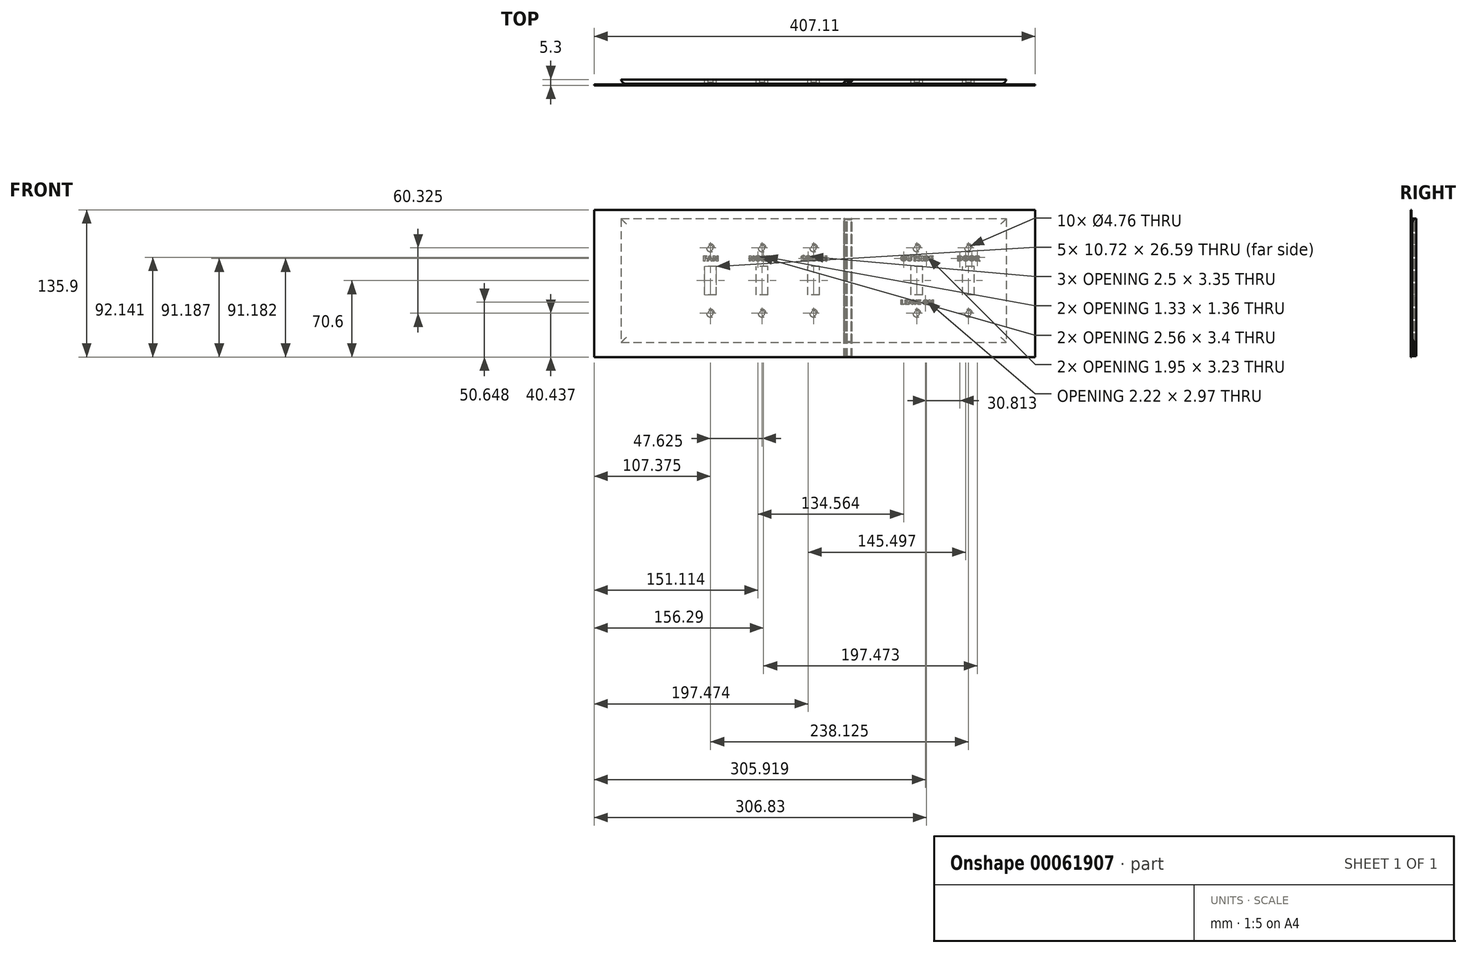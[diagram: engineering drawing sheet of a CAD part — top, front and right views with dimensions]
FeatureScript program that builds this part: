
annotation { "Feature Type Name" : "Feature", "Feature Type Description" : "" }
export const myFeature = defineFeature(function(context is Context, id is Id, definition is map)
    precondition{}
    {
        {
            var Q0;
            Q0=qCreatedBy(makeId("Front.planeOp"),FACE);
            var sketch = newSketch(context, id + "F0", { "sketchPlane" : qUnion([Q0])});
            skLineSegment(sketch, "E0.left", {"start": v(-320.68, 57.15) * mm, "end": v(-320.68, -57.15) * mm});
            skLineSegment(sketch, "E0.right", {"start": v(34.93, 57.15) * mm, "end": v(34.92, -57.15) * mm});
            skPoint(sketch, "E1", {"position": v(0, 57.15) * mm});
            skPoint(sketch, "E2", {"position": v(34.92, 0) * mm});
            skLineSegment(sketch, "E3.rect.bottom", {"start": v(5.36, -13.3) * mm, "end": v(-5.36, -13.3) * mm});
            skLineSegment(sketch, "E3.rect.top", {"start": v(5.36, 13.3) * mm, "end": v(-5.36, 13.3) * mm});
            skLineSegment(sketch, "E3.rect.left", {"start": v(5.36, -13.3) * mm, "end": v(5.36, 13.3) * mm});
            skLineSegment(sketch, "E3.rect.right", {"start": v(-5.36, -13.3) * mm, "end": v(-5.36, 13.3) * mm});
            skPoint(sketch, "E3.rect.middle", {"position": v(0, 0) * mm});
            skCircle(sketch, "E4", {"center": v(0, 30.16) * mm, "radius": 2.38 * mm});
            skLineSegment(sketch, "E5", {"start": v(43.2, 0) * mm, "end": v(-149.72, 0) * mm, "construction": true});
            skCircle(sketch, "E6.MirrorC", {"center": v(0, -30.16) * mm, "radius": 2.38 * mm});
            skLineSegment(sketch, "E7", {"start": v(-320.68, 57.15) * mm, "end": v(34.93, 57.15) * mm});
            skLineSegment(sketch, "E8", {"start": v(-320.68, -57.15) * mm, "end": v(34.92, -57.15) * mm});
            skLineSegment(sketch, "E9.rect.left", {"start": v(-42.27, -13.3) * mm, "end": v(-42.27, 13.3) * mm});
            skLineSegment(sketch, "E9.rect.right", {"start": v(-52.98, -13.3) * mm, "end": v(-52.98, 13.3) * mm});
            skPoint(sketch, "E9.rect.middle", {"position": v(-47.63, 0) * mm});
            skCircle(sketch, "E10", {"center": v(-47.63, 30.16) * mm, "radius": 2.38 * mm});
            skCircle(sketch, "E11.MirrorC", {"center": v(-47.63, -30.16) * mm, "radius": 2.38 * mm});
            skLineSegment(sketch, "E9.rect.bottom", {"start": v(-42.27, -13.3) * mm, "end": v(-52.98, -13.3) * mm});
            skLineSegment(sketch, "E9.rect.top", {"start": v(-42.27, 13.3) * mm, "end": v(-52.98, 13.3) * mm});
            skLineSegment(sketch, "E12.rect.left", {"start": v(-137.52, -13.3) * mm, "end": v(-137.52, 13.3) * mm});
            skLineSegment(sketch, "E12.rect.right", {"start": v(-148.23, -13.3) * mm, "end": v(-148.23, 13.3) * mm});
            skPoint(sketch, "E12.rect.middle", {"position": v(-142.88, 0) * mm});
            skCircle(sketch, "E13", {"center": v(-142.88, 30.16) * mm, "radius": 2.38 * mm});
            skCircle(sketch, "E14.MirrorC", {"center": v(-142.88, -30.16) * mm, "radius": 2.38 * mm});
            skLineSegment(sketch, "E12.rect.bottom", {"start": v(-137.52, -13.3) * mm, "end": v(-148.23, -13.3) * mm});
            skLineSegment(sketch, "E12.rect.top", {"start": v(-137.52, 13.3) * mm, "end": v(-148.23, 13.3) * mm});
            skLineSegment(sketch, "E15.rect.left", {"start": v(-185.14, -13.3) * mm, "end": v(-185.14, 13.3) * mm});
            skLineSegment(sketch, "E15.rect.right", {"start": v(-195.86, -13.3) * mm, "end": v(-195.86, 13.3) * mm});
            skPoint(sketch, "E15.rect.middle", {"position": v(-190.5, 0) * mm});
            skCircle(sketch, "E16", {"center": v(-190.5, 30.16) * mm, "radius": 2.38 * mm});
            skCircle(sketch, "E17.MirrorC", {"center": v(-190.5, -30.16) * mm, "radius": 2.38 * mm});
            skLineSegment(sketch, "E15.rect.bottom", {"start": v(-185.14, -13.3) * mm, "end": v(-195.86, -13.3) * mm});
            skLineSegment(sketch, "E15.rect.top", {"start": v(-185.14, 13.3) * mm, "end": v(-195.86, 13.3) * mm});
            skLineSegment(sketch, "E18.rect.left", {"start": v(-232.77, -13.3) * mm, "end": v(-232.77, 13.3) * mm});
            skLineSegment(sketch, "E18.rect.right", {"start": v(-243.48, -13.3) * mm, "end": v(-243.48, 13.3) * mm});
            skPoint(sketch, "E18.rect.middle", {"position": v(-238.13, 0) * mm});
            skCircle(sketch, "E19", {"center": v(-238.13, 30.16) * mm, "radius": 2.38 * mm});
            skCircle(sketch, "E20.MirrorC", {"center": v(-238.13, -30.16) * mm, "radius": 2.38 * mm});
            skLineSegment(sketch, "E18.rect.bottom", {"start": v(-232.77, -13.3) * mm, "end": v(-243.48, -13.3) * mm});
            skLineSegment(sketch, "E18.rect.top", {"start": v(-232.77, 13.3) * mm, "end": v(-243.48, 13.3) * mm});
            skLineSegment(sketch, "E21", {"start": v(-243.48, 13.3) * mm, "end": v(-195.86, 13.3) * mm, "construction": true});
            skLineSegment(sketch, "E22", {"start": v(-195.86, 13.3) * mm, "end": v(-148.23, 13.3) * mm, "construction": true});
            skLineSegment(sketch, "E23", {"start": v(-52.98, 13.3) * mm, "end": v(-5.36, 13.3) * mm, "construction": true});
            skSolve(sketch);
        }
        {
            var Q0;
            Q0=makeQuery(id+"F0.imprint","IMPRINT",FACE,{"disambiguationData":[TD([[makeQuery(id+"F0.imprint","IMPRINT",EDGE,{"derivedFrom":sQuery(id+"F0.wireOp",EDGE,"E0.left")}),1.0]])]});
            extrude(context, id + "F1", {"entities" : qUnion([Q0]), "depth" : 3.97 * mm});
        }
        {
            var Q0;
            Q0=makeQuery(id+"F1.opExtrude","SWEPT_FACE",FACE,{"disambiguationData":[OSD([sQuery(id+"F0.wireOp",EDGE,"E7")])]});
            var sketch = newSketch(context, id + "F2", { "sketchPlane" : qUnion([Q0])});
            skArc(sketch, "E24", {"start": v(-114.3, -1.98) * mm, "mid": v(-114.79, -2.98) * mm, "end": v(-114.3, -3.97) * mm});
            skArc(sketch, "E25", {"start": v(-107.95, -1.98) * mm, "mid": v(-107.46, -1) * mm, "end": v(-107.95, 0) * mm});
            skLineSegment(sketch, "E26", {"start": v(-111.12, 0) * mm, "end": v(-111.12, -3.97) * mm, "construction": true});
            skPoint(sketch, "E27", {"position": v(-111.12, -1.98) * mm});
            skLineSegment(sketch, "E28", {"start": v(-114.3, -1.98) * mm, "end": v(-113.53, -1.98) * mm, "construction": true});
            skLineSegment(sketch, "E29", {"start": v(-111.12, -1.98) * mm, "end": v(-108.72, -1.98) * mm, "construction": true});
            skLineSegment(sketch, "E30", {"start": v(-113.53, -1.98) * mm, "end": v(-111.12, -1.98) * mm, "construction": true});
            skLineSegment(sketch, "E31", {"start": v(-108.72, -1.98) * mm, "end": v(-107.95, -1.98) * mm, "construction": true});
            skLineSegment(sketch, "E32", {"start": v(-114.3, -1.98) * mm, "end": v(-113.53, -1.98) * mm});
            skLineSegment(sketch, "E33", {"start": v(-113.53, -1.98) * mm, "end": v(-113.29, -1.43) * mm});
            skLineSegment(sketch, "E34", {"start": v(-113.29, -1.43) * mm, "end": v(-112.27, -1.43) * mm});
            skLineSegment(sketch, "E35", {"start": v(-112.27, -1.43) * mm, "end": v(-111.95, -1.98) * mm});
            skLineSegment(sketch, "E36", {"start": v(-111.95, -1.98) * mm, "end": v(-107.95, -1.98) * mm});
            skArc(sketch, "E37.0", {"start": v(-114.36, -1.8) * mm, "mid": v(-114.96, -2.84) * mm, "end": v(-114.57, -3.97) * mm});
            skLineSegment(sketch, "E37.1", {"start": v(-114.36, -1.8) * mm, "end": v(-113.65, -1.8) * mm});
            skLineSegment(sketch, "E37.2", {"start": v(-113.65, -1.8) * mm, "end": v(-113.4, -1.25) * mm});
            skArc(sketch, "E37.3", {"start": v(-108.01, -1.8) * mm, "mid": v(-107.65, -0.82) * mm, "end": v(-108.3, 0) * mm});
            skLineSegment(sketch, "E37.4", {"start": v(-111.85, -1.8) * mm, "end": v(-108.01, -1.8) * mm});
            skLineSegment(sketch, "E37.5", {"start": v(-112.17, -1.25) * mm, "end": v(-111.85, -1.8) * mm});
            skLineSegment(sketch, "E37.6", {"start": v(-113.4, -1.25) * mm, "end": v(-112.17, -1.25) * mm});
            skLineSegment(sketch, "E38", {"start": v(-114.57, -3.97) * mm, "end": v(-114.3, -3.97) * mm});
            skLineSegment(sketch, "E39", {"start": v(-108.3, 0) * mm, "end": v(-107.95, 0) * mm});
            skSolve(sketch);
        }
        {
            var Q0;
            Q0 = qSketchRegion(id + "F2", true);
            extrude(context, id + "F3", {"entities" : qUnion([Q0]), "oppositeDirection" : true, "depth" : 127 * mm});
        }
        {
            var Q0;
            Q0=makeQuery(id+"F1.opExtrude","CAP_EDGE",EDGE,{"disambiguationData":[OSD([sQuery(id+"F0.wireOp",EDGE,"E7")])],"isStart":false});
            var Q1;
            Q1=makeQuery(id+"F1.opExtrude","CAP_EDGE",EDGE,{"disambiguationData":[OSD([sQuery(id+"F0.wireOp",EDGE,"E8")])],"isStart":false});
            var Q2;
            Q2=makeQuery(id+"F1.opExtrude","CAP_EDGE",EDGE,{"disambiguationData":[OSD([sQuery(id+"F0.wireOp",EDGE,"E0.right")])],"isStart":false});
            var Q3;
            Q3=makeQuery(id+"F1.opExtrude","CAP_EDGE",EDGE,{"disambiguationData":[OSD([sQuery(id+"F0.wireOp",EDGE,"E0.left")])],"isStart":false});
            fillet(context, id + "F4", {"entities" : qUnion([Q0, Q1, Q2, Q3]), "radius" : 5.08 * mm, "tangentPropagation" : true, "allowEdgeOverflow" : false});
        }
        {
            var Q0;
            Q0=makeQuery(id+"F3.opExtrude","SWEPT_BODY",BODY,{"disambiguationData":[OSD([sQuery(id+"F2.wireOp",EDGE,"E24"),sQuery(id+"F2.wireOp",EDGE,"E25"),sQuery(id+"F2.wireOp",EDGE,"E32"),sQuery(id+"F2.wireOp",EDGE,"E33"),sQuery(id+"F2.wireOp",EDGE,"E34"),sQuery(id+"F2.wireOp",EDGE,"E35"),sQuery(id+"F2.wireOp",EDGE,"E36"),sQuery(id+"F2.wireOp",EDGE,"E37.0"),sQuery(id+"F2.wireOp",EDGE,"E37.1"),sQuery(id+"F2.wireOp",EDGE,"E37.2"),sQuery(id+"F2.wireOp",EDGE,"E37.3"),sQuery(id+"F2.wireOp",EDGE,"E37.4"),sQuery(id+"F2.wireOp",EDGE,"E37.5"),sQuery(id+"F2.wireOp",EDGE,"E37.6"),sQuery(id+"F2.wireOp",EDGE,"E38"),sQuery(id+"F2.wireOp",EDGE,"E39")])]});
            var Q1;
            Q1=makeQuery(id+"F1.opExtrude","SWEPT_BODY",BODY,{"disambiguationData":[OSD([sQuery(id+"F0.wireOp",EDGE,"E0.right"),sQuery(id+"F0.wireOp",EDGE,"E3.rect.bottom"),sQuery(id+"F0.wireOp",EDGE,"E3.rect.top"),sQuery(id+"F0.wireOp",EDGE,"E3.rect.left"),sQuery(id+"F0.wireOp",EDGE,"E3.rect.right"),sQuery(id+"F0.wireOp",EDGE,"E4"),sQuery(id+"F0.wireOp",EDGE,"E6.MirrorC"),sQuery(id+"F0.wireOp",EDGE,"E7"),sQuery(id+"F0.wireOp",EDGE,"E8"),sQuery(id+"F0.wireOp",EDGE,"E9.rect.left"),sQuery(id+"F0.wireOp",EDGE,"E9.rect.right"),sQuery(id+"F0.wireOp",EDGE,"E10"),sQuery(id+"F0.wireOp",EDGE,"E11.MirrorC"),sQuery(id+"F0.wireOp",EDGE,"E9.rect.bottom"),sQuery(id+"F0.wireOp",EDGE,"E9.rect.top"),sQuery(id+"F0.wireOp",EDGE,"6Bv0av7S-DaCH-K0Nu-mwO3-w7JLu1CZrWGv")])]});
            booleanBodies(context, id + "F5", {"operationType" : BooleanOperationType.SUBTRACTION, "tools" : qUnion([Q0]), "targets" : qUnion([Q1]), "keepTools" : true});
        }
        {
            var Q0;
            Q0=makeQuery(id+"F1.opExtrude","CAP_EDGE",EDGE,{"disambiguationData":[OSD([sQuery(id+"F0.wireOp",EDGE,"E4")])],"isStart":false});
            var Q1;
            Q1=makeQuery(id+"F1.opExtrude","CAP_EDGE",EDGE,{"disambiguationData":[OSD([sQuery(id+"F0.wireOp",EDGE,"E10")])],"isStart":false});
            var Q2;
            Q2=makeQuery(id+"F1.opExtrude","CAP_EDGE",EDGE,{"disambiguationData":[OSD([sQuery(id+"F0.wireOp",EDGE,"E6.MirrorC")])],"isStart":false});
            var Q3;
            Q3=makeQuery(id+"F1.opExtrude","CAP_EDGE",EDGE,{"disambiguationData":[OSD([sQuery(id+"F0.wireOp",EDGE,"E11.MirrorC")])],"isStart":false});
            var Q4;
            Q4=makeQuery(id+"F1.opExtrude","CAP_EDGE",EDGE,{"disambiguationData":[OSD([sQuery(id+"F0.wireOp",EDGE,"E14.MirrorC")])],"isStart":false});
            var Q5;
            Q5=makeQuery(id+"F1.opExtrude","CAP_EDGE",EDGE,{"disambiguationData":[OSD([sQuery(id+"F0.wireOp",EDGE,"E17.MirrorC")])],"isStart":false});
            var Q6;
            Q6=makeQuery(id+"F1.opExtrude","CAP_EDGE",EDGE,{"disambiguationData":[OSD([sQuery(id+"F0.wireOp",EDGE,"E20.MirrorC")])],"isStart":false});
            var Q7;
            Q7=makeQuery(id+"F1.opExtrude","CAP_EDGE",EDGE,{"disambiguationData":[OSD([sQuery(id+"F0.wireOp",EDGE,"E16")])],"isStart":false});
            var Q8;
            Q8=makeQuery(id+"F1.opExtrude","CAP_EDGE",EDGE,{"disambiguationData":[OSD([sQuery(id+"F0.wireOp",EDGE,"E13")])],"isStart":false});
            var Q9;
            Q9=makeQuery(id+"F1.opExtrude","CAP_EDGE",EDGE,{"disambiguationData":[OSD([sQuery(id+"F0.wireOp",EDGE,"E19")])],"isStart":false});
            chamfer(context, id + "F6", {"entities" : qUnion([Q0, Q1, Q2, Q3, Q4, Q5, Q6, Q7, Q8, Q9]), "width" : 1.27 * mm, "tangentPropagation" : true});
        }
        {
            var Q0;
            {var subQ0=sQuery(id+"F0.wireOp",EDGE,"E17.MirrorC");var subQ1=sQuery(id+"F0.wireOp",EDGE,"E15.rect.bottom");var subQ2=sQuery(id+"F0.wireOp",EDGE,"E18.rect.bottom");var subQ3=sQuery(id+"F0.wireOp",EDGE,"E15.rect.left");var subQ4=sQuery(id+"F0.wireOp",EDGE,"E12.rect.top");var subQ5=sQuery(id+"F0.wireOp",EDGE,"E16");var subQ6=sQuery(id+"F0.wireOp",EDGE,"E20.MirrorC");var subQ7=sQuery(id+"F0.wireOp",EDGE,"E15.rect.right");var subQ8=sQuery(id+"F0.wireOp",EDGE,"E19");var subQ9=sQuery(id+"F0.wireOp",EDGE,"E12.rect.left");var subQ10=sQuery(id+"F0.wireOp",EDGE,"E18.rect.top");var subQ11=sQuery(id+"F0.wireOp",EDGE,"E12.rect.bottom");var subQ12=sQuery(id+"F0.wireOp",EDGE,"E12.rect.right");var subQ13=sQuery(id+"F0.wireOp",EDGE,"E13");var subQ14=sQuery(id+"F0.wireOp",EDGE,"E8");var subQ15=sQuery(id+"F0.wireOp",EDGE,"E14.MirrorC");var subQ16=sQuery(id+"F0.wireOp",EDGE,"E15.rect.top");var subQ17=sQuery(id+"F0.wireOp",EDGE,"E18.rect.left");var subQ18=sQuery(id+"F0.wireOp",EDGE,"E18.rect.right");var subQ19=sQuery(id+"F0.wireOp",EDGE,"E0.left");var subQ20=sQuery(id+"F0.wireOp",EDGE,"E7");Q0=makeQuery(id+"F5.opBoolean","SPLIT",FACE,{"disambiguationData":[TD([makeQuery(id+"F1.opExtrude","SWEPT_FACE",FACE,{"disambiguationData":[OSD([subQ9])]})])],"derivedFrom":makeQuery(id+"F1.opExtrude","CAP_FACE",FACE,{"disambiguationData":[OSD([subQ19,sQuery(id+"F0.wireOp",EDGE,"E0.right"),sQuery(id+"F0.wireOp",EDGE,"E3.rect.bottom"),sQuery(id+"F0.wireOp",EDGE,"E3.rect.top"),sQuery(id+"F0.wireOp",EDGE,"E3.rect.left"),sQuery(id+"F0.wireOp",EDGE,"E3.rect.right"),sQuery(id+"F0.wireOp",EDGE,"E4"),sQuery(id+"F0.wireOp",EDGE,"E6.MirrorC"),subQ20,subQ14,sQuery(id+"F0.wireOp",EDGE,"E9.rect.left"),sQuery(id+"F0.wireOp",EDGE,"E9.rect.right"),sQuery(id+"F0.wireOp",EDGE,"E10"),sQuery(id+"F0.wireOp",EDGE,"E11.MirrorC"),sQuery(id+"F0.wireOp",EDGE,"E9.rect.bottom"),sQuery(id+"F0.wireOp",EDGE,"E9.rect.top"),subQ9,subQ12,subQ13,subQ15,subQ11,subQ4,subQ3,subQ7,subQ5,subQ0,subQ1,subQ16,subQ17,subQ18,subQ8,subQ6,subQ2,subQ10])],"isStart":false})});}
            var sketch = newSketch(context, id + "F7", { "sketchPlane" : qUnion([Q0])});
            skText(sketch, "E40", { "text": "OUTSIDE", "fontName": "OpenSans-Bold.ttf"});
            skText(sketch, "E41", { "text": "LEAVE ON\n", "fontName": "OpenSans-Bold.ttf"});
            skText(sketch, "E42", { "text": "DOOR", "fontName": "OpenSans-Bold.ttf"});
            skText(sketch, "E43", { "text": "NORTH", "fontName": "OpenSans-Bold.ttf"});
            skText(sketch, "E44", { "text": "SOUTH\n", "fontName": "OpenSans-Bold.ttf"});
            skText(sketch, "E45", { "text": "FAN", "fontName": "OpenSans-Bold.ttf"});
            const initialGuessF7  = {"E40": [-0.06263, 0.01806, 1, 0, 0.00508], "E41": [-0.0627, -0.0222, 1, 0, 0.00452], "E42": [-0.01056, 0.01806, 1, 0, 0.00508], "E43": [-0.20293, 0.01806, 1, 0, 0.00508], "E44": [-0.15472, 0.01806, 1, 0, 0.00508], "E45": [-0.24505, 0.01806, 1, 0, 0.00508]};
            skSetInitialGuess(sketch, initialGuessF7);
            skSolve(sketch);
        }
        {
            var Q0;
            Q0 = qSketchRegion(id + "F7", true);
            extrude(context, id + "F8", {"entities" : qUnion([Q0]), "depth" : 0.89 * mm, "hasSecondDirection" : true, "secondDirectionOppositeDirection" : true, "secondDirectionDepth" : 0.25 * mm, "hasSecondDirectionDraft" : true, "secondDirectionDraftAngle" : 6 * degree});
        }
        {
            var Q0;
            Q0=makeQuery(id+"F8.split0.splitOp","SPLIT",BODY,{"derivedFrom":makeQuery(id+"F8.opExtrude","SWEPT_BODY",BODY,{"disambiguationData":[OSD([sQuery(id+"F7.wireOp",EDGE,"E40.sketch_text.stroke-0"),sQuery(id+"F7.wireOp",EDGE,"E40.sketch_text.stroke-1"),sQuery(id+"F7.wireOp",EDGE,"E40.sketch_text.stroke-2"),sQuery(id+"F7.wireOp",EDGE,"E40.sketch_text.stroke-3"),sQuery(id+"F7.wireOp",EDGE,"E40.sketch_text.stroke-4"),sQuery(id+"F7.wireOp",EDGE,"E40.sketch_text.stroke-5"),sQuery(id+"F7.wireOp",EDGE,"E40.sketch_text.stroke-6"),sQuery(id+"F7.wireOp",EDGE,"E40.sketch_text.stroke-7"),sQuery(id+"F7.wireOp",EDGE,"E40.sketch_text.stroke-8"),sQuery(id+"F7.wireOp",EDGE,"E40.sketch_text.stroke-9"),sQuery(id+"F7.wireOp",EDGE,"E40.sketch_text.stroke-10"),sQuery(id+"F7.wireOp",EDGE,"E40.sketch_text.stroke-11"),sQuery(id+"F7.wireOp",EDGE,"E40.sketch_text.stroke-12"),sQuery(id+"F7.wireOp",EDGE,"E40.sketch_text.stroke-13")])]})});
            var Q1;
            Q1=makeQuery(id+"F8.split1.splitOp","SPLIT",BODY,{"derivedFrom":makeQuery(id+"F8.opExtrude","SWEPT_BODY",BODY,{"disambiguationData":[OSD([sQuery(id+"F7.wireOp",EDGE,"E40.sketch_text.stroke-14"),sQuery(id+"F7.wireOp",EDGE,"E40.sketch_text.stroke-15"),sQuery(id+"F7.wireOp",EDGE,"E40.sketch_text.stroke-16"),sQuery(id+"F7.wireOp",EDGE,"E40.sketch_text.stroke-17"),sQuery(id+"F7.wireOp",EDGE,"E40.sketch_text.stroke-18"),sQuery(id+"F7.wireOp",EDGE,"E40.sketch_text.stroke-19"),sQuery(id+"F7.wireOp",EDGE,"E40.sketch_text.stroke-20"),sQuery(id+"F7.wireOp",EDGE,"E40.sketch_text.stroke-21"),sQuery(id+"F7.wireOp",EDGE,"E40.sketch_text.stroke-22"),sQuery(id+"F7.wireOp",EDGE,"E40.sketch_text.stroke-23"),sQuery(id+"F7.wireOp",EDGE,"E40.sketch_text.stroke-24"),sQuery(id+"F7.wireOp",EDGE,"E40.sketch_text.stroke-25"),sQuery(id+"F7.wireOp",EDGE,"E40.sketch_text.stroke-26"),sQuery(id+"F7.wireOp",EDGE,"E40.sketch_text.stroke-27"),sQuery(id+"F7.wireOp",EDGE,"E40.sketch_text.stroke-28")])]})});
            var Q2;
            Q2=makeQuery(id+"F8.split2.splitOp","SPLIT",BODY,{"derivedFrom":makeQuery(id+"F8.opExtrude","SWEPT_BODY",BODY,{"disambiguationData":[OSD([sQuery(id+"F7.wireOp",EDGE,"E40.sketch_text.stroke-29"),sQuery(id+"F7.wireOp",EDGE,"E40.sketch_text.stroke-30"),sQuery(id+"F7.wireOp",EDGE,"E40.sketch_text.stroke-31"),sQuery(id+"F7.wireOp",EDGE,"E40.sketch_text.stroke-32"),sQuery(id+"F7.wireOp",EDGE,"E40.sketch_text.stroke-33"),sQuery(id+"F7.wireOp",EDGE,"E40.sketch_text.stroke-34"),sQuery(id+"F7.wireOp",EDGE,"E40.sketch_text.stroke-35"),sQuery(id+"F7.wireOp",EDGE,"E40.sketch_text.stroke-36")])]})});
            var Q3;
            Q3=makeQuery(id+"F8.split3.splitOp","SPLIT",BODY,{"derivedFrom":makeQuery(id+"F8.opExtrude","SWEPT_BODY",BODY,{"disambiguationData":[OSD([sQuery(id+"F7.wireOp",EDGE,"E40.sketch_text.stroke-37"),sQuery(id+"F7.wireOp",EDGE,"E40.sketch_text.stroke-38"),sQuery(id+"F7.wireOp",EDGE,"E40.sketch_text.stroke-39"),sQuery(id+"F7.wireOp",EDGE,"E40.sketch_text.stroke-40"),sQuery(id+"F7.wireOp",EDGE,"E40.sketch_text.stroke-41"),sQuery(id+"F7.wireOp",EDGE,"E40.sketch_text.stroke-42"),sQuery(id+"F7.wireOp",EDGE,"E40.sketch_text.stroke-43"),sQuery(id+"F7.wireOp",EDGE,"E40.sketch_text.stroke-44"),sQuery(id+"F7.wireOp",EDGE,"E40.sketch_text.stroke-45"),sQuery(id+"F7.wireOp",EDGE,"E40.sketch_text.stroke-46"),sQuery(id+"F7.wireOp",EDGE,"E40.sketch_text.stroke-47"),sQuery(id+"F7.wireOp",EDGE,"E40.sketch_text.stroke-48"),sQuery(id+"F7.wireOp",EDGE,"E40.sketch_text.stroke-49"),sQuery(id+"F7.wireOp",EDGE,"E40.sketch_text.stroke-50"),sQuery(id+"F7.wireOp",EDGE,"E40.sketch_text.stroke-51"),sQuery(id+"F7.wireOp",EDGE,"E40.sketch_text.stroke-52"),sQuery(id+"F7.wireOp",EDGE,"E40.sketch_text.stroke-53"),sQuery(id+"F7.wireOp",EDGE,"E40.sketch_text.stroke-54"),sQuery(id+"F7.wireOp",EDGE,"E40.sketch_text.stroke-55"),sQuery(id+"F7.wireOp",EDGE,"E40.sketch_text.stroke-56"),sQuery(id+"F7.wireOp",EDGE,"E40.sketch_text.stroke-57"),sQuery(id+"F7.wireOp",EDGE,"E40.sketch_text.stroke-58"),sQuery(id+"F7.wireOp",EDGE,"E40.sketch_text.stroke-59"),sQuery(id+"F7.wireOp",EDGE,"E40.sketch_text.stroke-60"),sQuery(id+"F7.wireOp",EDGE,"E40.sketch_text.stroke-61"),sQuery(id+"F7.wireOp",EDGE,"E40.sketch_text.stroke-62"),sQuery(id+"F7.wireOp",EDGE,"E40.sketch_text.stroke-63"),sQuery(id+"F7.wireOp",EDGE,"E40.sketch_text.stroke-64")])]})});
            var Q4;
            Q4=makeQuery(id+"F8.split4.splitOp","SPLIT",BODY,{"derivedFrom":makeQuery(id+"F8.opExtrude","SWEPT_BODY",BODY,{"disambiguationData":[OSD([sQuery(id+"F7.wireOp",EDGE,"E40.sketch_text.stroke-65"),sQuery(id+"F7.wireOp",EDGE,"E40.sketch_text.stroke-66"),sQuery(id+"F7.wireOp",EDGE,"E40.sketch_text.stroke-67"),sQuery(id+"F7.wireOp",EDGE,"E40.sketch_text.stroke-68")])]})});
            var Q5;
            Q5=makeQuery(id+"F8.split5.splitOp","SPLIT",BODY,{"derivedFrom":makeQuery(id+"F8.opExtrude","SWEPT_BODY",BODY,{"disambiguationData":[OSD([sQuery(id+"F7.wireOp",EDGE,"E40.sketch_text.stroke-69"),sQuery(id+"F7.wireOp",EDGE,"E40.sketch_text.stroke-70"),sQuery(id+"F7.wireOp",EDGE,"E40.sketch_text.stroke-71"),sQuery(id+"F7.wireOp",EDGE,"E40.sketch_text.stroke-72"),sQuery(id+"F7.wireOp",EDGE,"E40.sketch_text.stroke-73"),sQuery(id+"F7.wireOp",EDGE,"E40.sketch_text.stroke-74"),sQuery(id+"F7.wireOp",EDGE,"E40.sketch_text.stroke-75"),sQuery(id+"F7.wireOp",EDGE,"E40.sketch_text.stroke-76"),sQuery(id+"F7.wireOp",EDGE,"E40.sketch_text.stroke-77"),sQuery(id+"F7.wireOp",EDGE,"E40.sketch_text.stroke-78"),sQuery(id+"F7.wireOp",EDGE,"E40.sketch_text.stroke-79"),sQuery(id+"F7.wireOp",EDGE,"E40.sketch_text.stroke-80")])]})});
            var Q6;
            Q6=makeQuery(id+"F8.split6.splitOp","SPLIT",BODY,{"derivedFrom":makeQuery(id+"F8.opExtrude","SWEPT_BODY",BODY,{"disambiguationData":[OSD([sQuery(id+"F7.wireOp",EDGE,"E40.sketch_text.stroke-81"),sQuery(id+"F7.wireOp",EDGE,"E40.sketch_text.stroke-82"),sQuery(id+"F7.wireOp",EDGE,"E40.sketch_text.stroke-83"),sQuery(id+"F7.wireOp",EDGE,"E40.sketch_text.stroke-84"),sQuery(id+"F7.wireOp",EDGE,"E40.sketch_text.stroke-85"),sQuery(id+"F7.wireOp",EDGE,"E40.sketch_text.stroke-86"),sQuery(id+"F7.wireOp",EDGE,"E40.sketch_text.stroke-87"),sQuery(id+"F7.wireOp",EDGE,"E40.sketch_text.stroke-88"),sQuery(id+"F7.wireOp",EDGE,"E40.sketch_text.stroke-89"),sQuery(id+"F7.wireOp",EDGE,"E40.sketch_text.stroke-90"),sQuery(id+"F7.wireOp",EDGE,"E40.sketch_text.stroke-91"),sQuery(id+"F7.wireOp",EDGE,"E40.sketch_text.stroke-92")])]})});
            var Q7;
            Q7=makeQuery(id+"F8.split7.splitOp","SPLIT",BODY,{"derivedFrom":makeQuery(id+"F8.opExtrude","SWEPT_BODY",BODY,{"disambiguationData":[OSD([sQuery(id+"F7.wireOp",EDGE,"E41.sketch_text.stroke-0"),sQuery(id+"F7.wireOp",EDGE,"E41.sketch_text.stroke-1"),sQuery(id+"F7.wireOp",EDGE,"E41.sketch_text.stroke-2"),sQuery(id+"F7.wireOp",EDGE,"E41.sketch_text.stroke-3"),sQuery(id+"F7.wireOp",EDGE,"E41.sketch_text.stroke-4"),sQuery(id+"F7.wireOp",EDGE,"E41.sketch_text.stroke-5")])]})});
            var Q8;
            Q8=makeQuery(id+"F8.split8.splitOp","SPLIT",BODY,{"derivedFrom":makeQuery(id+"F8.opExtrude","SWEPT_BODY",BODY,{"disambiguationData":[OSD([sQuery(id+"F7.wireOp",EDGE,"E41.sketch_text.stroke-6"),sQuery(id+"F7.wireOp",EDGE,"E41.sketch_text.stroke-7"),sQuery(id+"F7.wireOp",EDGE,"E41.sketch_text.stroke-8"),sQuery(id+"F7.wireOp",EDGE,"E41.sketch_text.stroke-9"),sQuery(id+"F7.wireOp",EDGE,"E41.sketch_text.stroke-10"),sQuery(id+"F7.wireOp",EDGE,"E41.sketch_text.stroke-11"),sQuery(id+"F7.wireOp",EDGE,"E41.sketch_text.stroke-12"),sQuery(id+"F7.wireOp",EDGE,"E41.sketch_text.stroke-13"),sQuery(id+"F7.wireOp",EDGE,"E41.sketch_text.stroke-14"),sQuery(id+"F7.wireOp",EDGE,"E41.sketch_text.stroke-15"),sQuery(id+"F7.wireOp",EDGE,"E41.sketch_text.stroke-16"),sQuery(id+"F7.wireOp",EDGE,"E41.sketch_text.stroke-17")])]})});
            var Q9;
            Q9=makeQuery(id+"F8.split9.splitOp","SPLIT",BODY,{"derivedFrom":makeQuery(id+"F8.opExtrude","SWEPT_BODY",BODY,{"disambiguationData":[OSD([sQuery(id+"F7.wireOp",EDGE,"E41.sketch_text.stroke-18"),sQuery(id+"F7.wireOp",EDGE,"E41.sketch_text.stroke-19"),sQuery(id+"F7.wireOp",EDGE,"E41.sketch_text.stroke-20"),sQuery(id+"F7.wireOp",EDGE,"E41.sketch_text.stroke-21"),sQuery(id+"F7.wireOp",EDGE,"E41.sketch_text.stroke-22"),sQuery(id+"F7.wireOp",EDGE,"E41.sketch_text.stroke-23"),sQuery(id+"F7.wireOp",EDGE,"E41.sketch_text.stroke-24"),sQuery(id+"F7.wireOp",EDGE,"E41.sketch_text.stroke-25"),sQuery(id+"F7.wireOp",EDGE,"E41.sketch_text.stroke-26"),sQuery(id+"F7.wireOp",EDGE,"E41.sketch_text.stroke-27"),sQuery(id+"F7.wireOp",EDGE,"E41.sketch_text.stroke-28"),sQuery(id+"F7.wireOp",EDGE,"E41.sketch_text.stroke-29")])]})});
            var Q10;
            Q10=makeQuery(id+"F8.split10.splitOp","SPLIT",BODY,{"derivedFrom":makeQuery(id+"F8.opExtrude","SWEPT_BODY",BODY,{"disambiguationData":[OSD([sQuery(id+"F7.wireOp",EDGE,"E41.sketch_text.stroke-30"),sQuery(id+"F7.wireOp",EDGE,"E41.sketch_text.stroke-31"),sQuery(id+"F7.wireOp",EDGE,"E41.sketch_text.stroke-32"),sQuery(id+"F7.wireOp",EDGE,"E41.sketch_text.stroke-33"),sQuery(id+"F7.wireOp",EDGE,"E41.sketch_text.stroke-34"),sQuery(id+"F7.wireOp",EDGE,"E41.sketch_text.stroke-35"),sQuery(id+"F7.wireOp",EDGE,"E41.sketch_text.stroke-36"),sQuery(id+"F7.wireOp",EDGE,"E41.sketch_text.stroke-37"),sQuery(id+"F7.wireOp",EDGE,"E41.sketch_text.stroke-38"),sQuery(id+"F7.wireOp",EDGE,"E41.sketch_text.stroke-39")])]})});
            var Q11;
            Q11=makeQuery(id+"F8.split11.splitOp","SPLIT",BODY,{"derivedFrom":makeQuery(id+"F8.opExtrude","SWEPT_BODY",BODY,{"disambiguationData":[OSD([sQuery(id+"F7.wireOp",EDGE,"E41.sketch_text.stroke-40"),sQuery(id+"F7.wireOp",EDGE,"E41.sketch_text.stroke-41"),sQuery(id+"F7.wireOp",EDGE,"E41.sketch_text.stroke-42"),sQuery(id+"F7.wireOp",EDGE,"E41.sketch_text.stroke-43"),sQuery(id+"F7.wireOp",EDGE,"E41.sketch_text.stroke-44"),sQuery(id+"F7.wireOp",EDGE,"E41.sketch_text.stroke-45"),sQuery(id+"F7.wireOp",EDGE,"E41.sketch_text.stroke-46"),sQuery(id+"F7.wireOp",EDGE,"E41.sketch_text.stroke-47"),sQuery(id+"F7.wireOp",EDGE,"E41.sketch_text.stroke-48"),sQuery(id+"F7.wireOp",EDGE,"E41.sketch_text.stroke-49"),sQuery(id+"F7.wireOp",EDGE,"E41.sketch_text.stroke-50"),sQuery(id+"F7.wireOp",EDGE,"E41.sketch_text.stroke-51")])]})});
            var Q12;
            Q12=makeQuery(id+"F8.split12.splitOp","SPLIT",BODY,{"derivedFrom":makeQuery(id+"F8.opExtrude","SWEPT_BODY",BODY,{"disambiguationData":[OSD([sQuery(id+"F7.wireOp",EDGE,"E41.sketch_text.stroke-52"),sQuery(id+"F7.wireOp",EDGE,"E41.sketch_text.stroke-53"),sQuery(id+"F7.wireOp",EDGE,"E41.sketch_text.stroke-54"),sQuery(id+"F7.wireOp",EDGE,"E41.sketch_text.stroke-55"),sQuery(id+"F7.wireOp",EDGE,"E41.sketch_text.stroke-56"),sQuery(id+"F7.wireOp",EDGE,"E41.sketch_text.stroke-57"),sQuery(id+"F7.wireOp",EDGE,"E41.sketch_text.stroke-58"),sQuery(id+"F7.wireOp",EDGE,"E41.sketch_text.stroke-59"),sQuery(id+"F7.wireOp",EDGE,"E41.sketch_text.stroke-60"),sQuery(id+"F7.wireOp",EDGE,"E41.sketch_text.stroke-61"),sQuery(id+"F7.wireOp",EDGE,"E41.sketch_text.stroke-62"),sQuery(id+"F7.wireOp",EDGE,"E41.sketch_text.stroke-63"),sQuery(id+"F7.wireOp",EDGE,"E41.sketch_text.stroke-64"),sQuery(id+"F7.wireOp",EDGE,"E41.sketch_text.stroke-65")])]})});
            var Q13;
            Q13=makeQuery(id+"F8.split13.splitOp","SPLIT",BODY,{"derivedFrom":makeQuery(id+"F8.opExtrude","SWEPT_BODY",BODY,{"disambiguationData":[OSD([sQuery(id+"F7.wireOp",EDGE,"E41.sketch_text.stroke-66"),sQuery(id+"F7.wireOp",EDGE,"E41.sketch_text.stroke-67"),sQuery(id+"F7.wireOp",EDGE,"E41.sketch_text.stroke-68"),sQuery(id+"F7.wireOp",EDGE,"E41.sketch_text.stroke-69"),sQuery(id+"F7.wireOp",EDGE,"E41.sketch_text.stroke-70"),sQuery(id+"F7.wireOp",EDGE,"E41.sketch_text.stroke-71"),sQuery(id+"F7.wireOp",EDGE,"E41.sketch_text.stroke-72"),sQuery(id+"F7.wireOp",EDGE,"E41.sketch_text.stroke-73"),sQuery(id+"F7.wireOp",EDGE,"E41.sketch_text.stroke-74"),sQuery(id+"F7.wireOp",EDGE,"E41.sketch_text.stroke-75"),sQuery(id+"F7.wireOp",EDGE,"E41.sketch_text.stroke-76"),sQuery(id+"F7.wireOp",EDGE,"E41.sketch_text.stroke-77"),sQuery(id+"F7.wireOp",EDGE,"E41.sketch_text.stroke-78"),sQuery(id+"F7.wireOp",EDGE,"E41.sketch_text.stroke-79")])]})});
            var Q14;
            Q14=makeQuery(id+"F8.split14.splitOp","SPLIT",BODY,{"derivedFrom":makeQuery(id+"F8.opExtrude","SWEPT_BODY",BODY,{"disambiguationData":[OSD([sQuery(id+"F7.wireOp",EDGE,"E42.sketch_text.stroke-0"),sQuery(id+"F7.wireOp",EDGE,"E42.sketch_text.stroke-1"),sQuery(id+"F7.wireOp",EDGE,"E42.sketch_text.stroke-2"),sQuery(id+"F7.wireOp",EDGE,"E42.sketch_text.stroke-3"),sQuery(id+"F7.wireOp",EDGE,"E42.sketch_text.stroke-4"),sQuery(id+"F7.wireOp",EDGE,"E42.sketch_text.stroke-5"),sQuery(id+"F7.wireOp",EDGE,"E42.sketch_text.stroke-6"),sQuery(id+"F7.wireOp",EDGE,"E42.sketch_text.stroke-7"),sQuery(id+"F7.wireOp",EDGE,"E42.sketch_text.stroke-8"),sQuery(id+"F7.wireOp",EDGE,"E42.sketch_text.stroke-9"),sQuery(id+"F7.wireOp",EDGE,"E42.sketch_text.stroke-10"),sQuery(id+"F7.wireOp",EDGE,"E42.sketch_text.stroke-11")])]})});
            var Q15;
            Q15=makeQuery(id+"F8.split15.splitOp","SPLIT",BODY,{"derivedFrom":makeQuery(id+"F8.opExtrude","SWEPT_BODY",BODY,{"disambiguationData":[OSD([sQuery(id+"F7.wireOp",EDGE,"E42.sketch_text.stroke-12"),sQuery(id+"F7.wireOp",EDGE,"E42.sketch_text.stroke-13"),sQuery(id+"F7.wireOp",EDGE,"E42.sketch_text.stroke-14"),sQuery(id+"F7.wireOp",EDGE,"E42.sketch_text.stroke-15"),sQuery(id+"F7.wireOp",EDGE,"E42.sketch_text.stroke-16"),sQuery(id+"F7.wireOp",EDGE,"E42.sketch_text.stroke-17"),sQuery(id+"F7.wireOp",EDGE,"E42.sketch_text.stroke-18"),sQuery(id+"F7.wireOp",EDGE,"E42.sketch_text.stroke-19"),sQuery(id+"F7.wireOp",EDGE,"E42.sketch_text.stroke-20"),sQuery(id+"F7.wireOp",EDGE,"E42.sketch_text.stroke-21"),sQuery(id+"F7.wireOp",EDGE,"E42.sketch_text.stroke-22"),sQuery(id+"F7.wireOp",EDGE,"E42.sketch_text.stroke-23"),sQuery(id+"F7.wireOp",EDGE,"E42.sketch_text.stroke-24"),sQuery(id+"F7.wireOp",EDGE,"E42.sketch_text.stroke-25")])]})});
            var Q16;
            Q16=makeQuery(id+"F8.split16.splitOp","SPLIT",BODY,{"derivedFrom":makeQuery(id+"F8.opExtrude","SWEPT_BODY",BODY,{"disambiguationData":[OSD([sQuery(id+"F7.wireOp",EDGE,"E42.sketch_text.stroke-26"),sQuery(id+"F7.wireOp",EDGE,"E42.sketch_text.stroke-27"),sQuery(id+"F7.wireOp",EDGE,"E42.sketch_text.stroke-28"),sQuery(id+"F7.wireOp",EDGE,"E42.sketch_text.stroke-29"),sQuery(id+"F7.wireOp",EDGE,"E42.sketch_text.stroke-30"),sQuery(id+"F7.wireOp",EDGE,"E42.sketch_text.stroke-31"),sQuery(id+"F7.wireOp",EDGE,"E42.sketch_text.stroke-32"),sQuery(id+"F7.wireOp",EDGE,"E42.sketch_text.stroke-33"),sQuery(id+"F7.wireOp",EDGE,"E42.sketch_text.stroke-34"),sQuery(id+"F7.wireOp",EDGE,"E42.sketch_text.stroke-35"),sQuery(id+"F7.wireOp",EDGE,"E42.sketch_text.stroke-36"),sQuery(id+"F7.wireOp",EDGE,"E42.sketch_text.stroke-37"),sQuery(id+"F7.wireOp",EDGE,"E42.sketch_text.stroke-38"),sQuery(id+"F7.wireOp",EDGE,"E42.sketch_text.stroke-39")])]})});
            var Q17;
            Q17=makeQuery(id+"F8.split17.splitOp","SPLIT",BODY,{"derivedFrom":makeQuery(id+"F8.opExtrude","SWEPT_BODY",BODY,{"disambiguationData":[OSD([sQuery(id+"F7.wireOp",EDGE,"E42.sketch_text.stroke-40"),sQuery(id+"F7.wireOp",EDGE,"E42.sketch_text.stroke-41"),sQuery(id+"F7.wireOp",EDGE,"E42.sketch_text.stroke-42"),sQuery(id+"F7.wireOp",EDGE,"E42.sketch_text.stroke-43"),sQuery(id+"F7.wireOp",EDGE,"E42.sketch_text.stroke-44"),sQuery(id+"F7.wireOp",EDGE,"E42.sketch_text.stroke-45"),sQuery(id+"F7.wireOp",EDGE,"E42.sketch_text.stroke-46"),sQuery(id+"F7.wireOp",EDGE,"E42.sketch_text.stroke-47"),sQuery(id+"F7.wireOp",EDGE,"E42.sketch_text.stroke-48"),sQuery(id+"F7.wireOp",EDGE,"E42.sketch_text.stroke-49"),sQuery(id+"F7.wireOp",EDGE,"E42.sketch_text.stroke-50"),sQuery(id+"F7.wireOp",EDGE,"E42.sketch_text.stroke-51"),sQuery(id+"F7.wireOp",EDGE,"E42.sketch_text.stroke-52"),sQuery(id+"F7.wireOp",EDGE,"E42.sketch_text.stroke-53"),sQuery(id+"F7.wireOp",EDGE,"E42.sketch_text.stroke-54"),sQuery(id+"F7.wireOp",EDGE,"E42.sketch_text.stroke-55"),sQuery(id+"F7.wireOp",EDGE,"E42.sketch_text.stroke-56"),sQuery(id+"F7.wireOp",EDGE,"E42.sketch_text.stroke-57"),sQuery(id+"F7.wireOp",EDGE,"E42.sketch_text.stroke-58")])]})});
            var Q18;
            Q18=makeQuery(id+"F5.opBoolean","SPLIT",BODY,{"disambiguationData":[OD(0.0)],"derivedFrom":makeQuery(id+"F1.opExtrude","SWEPT_BODY",BODY,{"disambiguationData":[OSD([sQuery(id+"F0.wireOp",EDGE,"E0.left"),sQuery(id+"F0.wireOp",EDGE,"E0.right"),sQuery(id+"F0.wireOp",EDGE,"E3.rect.bottom"),sQuery(id+"F0.wireOp",EDGE,"E3.rect.top"),sQuery(id+"F0.wireOp",EDGE,"E3.rect.left"),sQuery(id+"F0.wireOp",EDGE,"E3.rect.right"),sQuery(id+"F0.wireOp",EDGE,"E4"),sQuery(id+"F0.wireOp",EDGE,"E6.MirrorC"),sQuery(id+"F0.wireOp",EDGE,"E7"),sQuery(id+"F0.wireOp",EDGE,"E8"),sQuery(id+"F0.wireOp",EDGE,"E9.rect.left"),sQuery(id+"F0.wireOp",EDGE,"E9.rect.right"),sQuery(id+"F0.wireOp",EDGE,"E10"),sQuery(id+"F0.wireOp",EDGE,"E11.MirrorC"),sQuery(id+"F0.wireOp",EDGE,"E9.rect.bottom"),sQuery(id+"F0.wireOp",EDGE,"E9.rect.top"),sQuery(id+"F0.wireOp",EDGE,"E12.rect.left"),sQuery(id+"F0.wireOp",EDGE,"E12.rect.right"),sQuery(id+"F0.wireOp",EDGE,"E13"),sQuery(id+"F0.wireOp",EDGE,"E14.MirrorC"),sQuery(id+"F0.wireOp",EDGE,"E12.rect.bottom"),sQuery(id+"F0.wireOp",EDGE,"E12.rect.top"),sQuery(id+"F0.wireOp",EDGE,"E15.rect.left"),sQuery(id+"F0.wireOp",EDGE,"E15.rect.right"),sQuery(id+"F0.wireOp",EDGE,"E16"),sQuery(id+"F0.wireOp",EDGE,"E17.MirrorC"),sQuery(id+"F0.wireOp",EDGE,"E15.rect.bottom"),sQuery(id+"F0.wireOp",EDGE,"E15.rect.top"),sQuery(id+"F0.wireOp",EDGE,"E18.rect.left"),sQuery(id+"F0.wireOp",EDGE,"E18.rect.right"),sQuery(id+"F0.wireOp",EDGE,"E19"),sQuery(id+"F0.wireOp",EDGE,"E20.MirrorC"),sQuery(id+"F0.wireOp",EDGE,"E18.rect.bottom"),sQuery(id+"F0.wireOp",EDGE,"E18.rect.top")])]})});
            booleanBodies(context, id + "F9", {"operationType" : BooleanOperationType.SUBTRACTION, "tools" : qUnion([Q0, Q1, Q2, Q3, Q4, Q5, Q6, Q7, Q8, Q9, Q10, Q11, Q12, Q13, Q14, Q15, Q16, Q17]), "targets" : qUnion([Q18]), "keepTools" : true});
        }
        {
            var Q0;
            Q0=makeQuery(id+"F8.split18.splitOp","SPLIT",BODY,{"derivedFrom":makeQuery(id+"F8.opExtrude","SWEPT_BODY",BODY,{"disambiguationData":[OSD([sQuery(id+"F7.wireOp",EDGE,"E43.sketch_text.stroke-0"),sQuery(id+"F7.wireOp",EDGE,"E43.sketch_text.stroke-1"),sQuery(id+"F7.wireOp",EDGE,"E43.sketch_text.stroke-2"),sQuery(id+"F7.wireOp",EDGE,"E43.sketch_text.stroke-3"),sQuery(id+"F7.wireOp",EDGE,"E43.sketch_text.stroke-4"),sQuery(id+"F7.wireOp",EDGE,"E43.sketch_text.stroke-5"),sQuery(id+"F7.wireOp",EDGE,"E43.sketch_text.stroke-6"),sQuery(id+"F7.wireOp",EDGE,"E43.sketch_text.stroke-7"),sQuery(id+"F7.wireOp",EDGE,"E43.sketch_text.stroke-8"),sQuery(id+"F7.wireOp",EDGE,"E43.sketch_text.stroke-9"),sQuery(id+"F7.wireOp",EDGE,"E43.sketch_text.stroke-10"),sQuery(id+"F7.wireOp",EDGE,"E43.sketch_text.stroke-11"),sQuery(id+"F7.wireOp",EDGE,"E43.sketch_text.stroke-12"),sQuery(id+"F7.wireOp",EDGE,"E43.sketch_text.stroke-13")])]})});
            var Q1;
            Q1=makeQuery(id+"F8.split19.splitOp","SPLIT",BODY,{"derivedFrom":makeQuery(id+"F8.opExtrude","SWEPT_BODY",BODY,{"disambiguationData":[OSD([sQuery(id+"F7.wireOp",EDGE,"E43.sketch_text.stroke-14"),sQuery(id+"F7.wireOp",EDGE,"E43.sketch_text.stroke-15"),sQuery(id+"F7.wireOp",EDGE,"E43.sketch_text.stroke-16"),sQuery(id+"F7.wireOp",EDGE,"E43.sketch_text.stroke-17"),sQuery(id+"F7.wireOp",EDGE,"E43.sketch_text.stroke-18"),sQuery(id+"F7.wireOp",EDGE,"E43.sketch_text.stroke-19"),sQuery(id+"F7.wireOp",EDGE,"E43.sketch_text.stroke-20"),sQuery(id+"F7.wireOp",EDGE,"E43.sketch_text.stroke-21"),sQuery(id+"F7.wireOp",EDGE,"E43.sketch_text.stroke-22"),sQuery(id+"F7.wireOp",EDGE,"E43.sketch_text.stroke-23"),sQuery(id+"F7.wireOp",EDGE,"E43.sketch_text.stroke-24"),sQuery(id+"F7.wireOp",EDGE,"E43.sketch_text.stroke-25"),sQuery(id+"F7.wireOp",EDGE,"E43.sketch_text.stroke-26"),sQuery(id+"F7.wireOp",EDGE,"E43.sketch_text.stroke-27")])]})});
            var Q2;
            Q2=makeQuery(id+"F8.split20.splitOp","SPLIT",BODY,{"derivedFrom":makeQuery(id+"F8.opExtrude","SWEPT_BODY",BODY,{"disambiguationData":[OSD([sQuery(id+"F7.wireOp",EDGE,"E43.sketch_text.stroke-28"),sQuery(id+"F7.wireOp",EDGE,"E43.sketch_text.stroke-29"),sQuery(id+"F7.wireOp",EDGE,"E43.sketch_text.stroke-30"),sQuery(id+"F7.wireOp",EDGE,"E43.sketch_text.stroke-31"),sQuery(id+"F7.wireOp",EDGE,"E43.sketch_text.stroke-32"),sQuery(id+"F7.wireOp",EDGE,"E43.sketch_text.stroke-33"),sQuery(id+"F7.wireOp",EDGE,"E43.sketch_text.stroke-34"),sQuery(id+"F7.wireOp",EDGE,"E43.sketch_text.stroke-35"),sQuery(id+"F7.wireOp",EDGE,"E43.sketch_text.stroke-36"),sQuery(id+"F7.wireOp",EDGE,"E43.sketch_text.stroke-37"),sQuery(id+"F7.wireOp",EDGE,"E43.sketch_text.stroke-38"),sQuery(id+"F7.wireOp",EDGE,"E43.sketch_text.stroke-39"),sQuery(id+"F7.wireOp",EDGE,"E43.sketch_text.stroke-40"),sQuery(id+"F7.wireOp",EDGE,"E43.sketch_text.stroke-41"),sQuery(id+"F7.wireOp",EDGE,"E43.sketch_text.stroke-42"),sQuery(id+"F7.wireOp",EDGE,"E43.sketch_text.stroke-43"),sQuery(id+"F7.wireOp",EDGE,"E43.sketch_text.stroke-44"),sQuery(id+"F7.wireOp",EDGE,"E43.sketch_text.stroke-45"),sQuery(id+"F7.wireOp",EDGE,"E43.sketch_text.stroke-46")])]})});
            var Q3;
            Q3=makeQuery(id+"F8.split21.splitOp","SPLIT",BODY,{"derivedFrom":makeQuery(id+"F8.opExtrude","SWEPT_BODY",BODY,{"disambiguationData":[OSD([sQuery(id+"F7.wireOp",EDGE,"E43.sketch_text.stroke-47"),sQuery(id+"F7.wireOp",EDGE,"E43.sketch_text.stroke-48"),sQuery(id+"F7.wireOp",EDGE,"E43.sketch_text.stroke-49"),sQuery(id+"F7.wireOp",EDGE,"E43.sketch_text.stroke-50"),sQuery(id+"F7.wireOp",EDGE,"E43.sketch_text.stroke-51"),sQuery(id+"F7.wireOp",EDGE,"E43.sketch_text.stroke-52"),sQuery(id+"F7.wireOp",EDGE,"E43.sketch_text.stroke-53"),sQuery(id+"F7.wireOp",EDGE,"E43.sketch_text.stroke-54")])]})});
            var Q4;
            Q4=makeQuery(id+"F8.split22.splitOp","SPLIT",BODY,{"derivedFrom":makeQuery(id+"F8.opExtrude","SWEPT_BODY",BODY,{"disambiguationData":[OSD([sQuery(id+"F7.wireOp",EDGE,"E43.sketch_text.stroke-55"),sQuery(id+"F7.wireOp",EDGE,"E43.sketch_text.stroke-56"),sQuery(id+"F7.wireOp",EDGE,"E43.sketch_text.stroke-57"),sQuery(id+"F7.wireOp",EDGE,"E43.sketch_text.stroke-58"),sQuery(id+"F7.wireOp",EDGE,"E43.sketch_text.stroke-59"),sQuery(id+"F7.wireOp",EDGE,"E43.sketch_text.stroke-60"),sQuery(id+"F7.wireOp",EDGE,"E43.sketch_text.stroke-61"),sQuery(id+"F7.wireOp",EDGE,"E43.sketch_text.stroke-62"),sQuery(id+"F7.wireOp",EDGE,"E43.sketch_text.stroke-63"),sQuery(id+"F7.wireOp",EDGE,"E43.sketch_text.stroke-64"),sQuery(id+"F7.wireOp",EDGE,"E43.sketch_text.stroke-65"),sQuery(id+"F7.wireOp",EDGE,"E43.sketch_text.stroke-66")])]})});
            var Q5;
            Q5=makeQuery(id+"F8.split23.splitOp","SPLIT",BODY,{"derivedFrom":makeQuery(id+"F8.opExtrude","SWEPT_BODY",BODY,{"disambiguationData":[OSD([sQuery(id+"F7.wireOp",EDGE,"E44.sketch_text.stroke-0"),sQuery(id+"F7.wireOp",EDGE,"E44.sketch_text.stroke-1"),sQuery(id+"F7.wireOp",EDGE,"E44.sketch_text.stroke-2"),sQuery(id+"F7.wireOp",EDGE,"E44.sketch_text.stroke-3"),sQuery(id+"F7.wireOp",EDGE,"E44.sketch_text.stroke-4"),sQuery(id+"F7.wireOp",EDGE,"E44.sketch_text.stroke-5"),sQuery(id+"F7.wireOp",EDGE,"E44.sketch_text.stroke-6"),sQuery(id+"F7.wireOp",EDGE,"E44.sketch_text.stroke-7"),sQuery(id+"F7.wireOp",EDGE,"E44.sketch_text.stroke-8"),sQuery(id+"F7.wireOp",EDGE,"E44.sketch_text.stroke-9"),sQuery(id+"F7.wireOp",EDGE,"E44.sketch_text.stroke-10"),sQuery(id+"F7.wireOp",EDGE,"E44.sketch_text.stroke-11"),sQuery(id+"F7.wireOp",EDGE,"E44.sketch_text.stroke-12"),sQuery(id+"F7.wireOp",EDGE,"E44.sketch_text.stroke-13"),sQuery(id+"F7.wireOp",EDGE,"E44.sketch_text.stroke-14"),sQuery(id+"F7.wireOp",EDGE,"E44.sketch_text.stroke-15"),sQuery(id+"F7.wireOp",EDGE,"E44.sketch_text.stroke-16"),sQuery(id+"F7.wireOp",EDGE,"E44.sketch_text.stroke-17"),sQuery(id+"F7.wireOp",EDGE,"E44.sketch_text.stroke-18"),sQuery(id+"F7.wireOp",EDGE,"E44.sketch_text.stroke-19"),sQuery(id+"F7.wireOp",EDGE,"E44.sketch_text.stroke-20"),sQuery(id+"F7.wireOp",EDGE,"E44.sketch_text.stroke-21"),sQuery(id+"F7.wireOp",EDGE,"E44.sketch_text.stroke-22"),sQuery(id+"F7.wireOp",EDGE,"E44.sketch_text.stroke-23"),sQuery(id+"F7.wireOp",EDGE,"E44.sketch_text.stroke-24"),sQuery(id+"F7.wireOp",EDGE,"E44.sketch_text.stroke-25"),sQuery(id+"F7.wireOp",EDGE,"E44.sketch_text.stroke-26"),sQuery(id+"F7.wireOp",EDGE,"E44.sketch_text.stroke-27")])]})});
            var Q6;
            Q6=makeQuery(id+"F8.split24.splitOp","SPLIT",BODY,{"derivedFrom":makeQuery(id+"F8.opExtrude","SWEPT_BODY",BODY,{"disambiguationData":[OSD([sQuery(id+"F7.wireOp",EDGE,"E44.sketch_text.stroke-28"),sQuery(id+"F7.wireOp",EDGE,"E44.sketch_text.stroke-29"),sQuery(id+"F7.wireOp",EDGE,"E44.sketch_text.stroke-30"),sQuery(id+"F7.wireOp",EDGE,"E44.sketch_text.stroke-31"),sQuery(id+"F7.wireOp",EDGE,"E44.sketch_text.stroke-32"),sQuery(id+"F7.wireOp",EDGE,"E44.sketch_text.stroke-33"),sQuery(id+"F7.wireOp",EDGE,"E44.sketch_text.stroke-34"),sQuery(id+"F7.wireOp",EDGE,"E44.sketch_text.stroke-35"),sQuery(id+"F7.wireOp",EDGE,"E44.sketch_text.stroke-36"),sQuery(id+"F7.wireOp",EDGE,"E44.sketch_text.stroke-37"),sQuery(id+"F7.wireOp",EDGE,"E44.sketch_text.stroke-38"),sQuery(id+"F7.wireOp",EDGE,"E44.sketch_text.stroke-39"),sQuery(id+"F7.wireOp",EDGE,"E44.sketch_text.stroke-40"),sQuery(id+"F7.wireOp",EDGE,"E44.sketch_text.stroke-41")])]})});
            var Q7;
            Q7=makeQuery(id+"F8.split25.splitOp","SPLIT",BODY,{"derivedFrom":makeQuery(id+"F8.opExtrude","SWEPT_BODY",BODY,{"disambiguationData":[OSD([sQuery(id+"F7.wireOp",EDGE,"E44.sketch_text.stroke-42"),sQuery(id+"F7.wireOp",EDGE,"E44.sketch_text.stroke-43"),sQuery(id+"F7.wireOp",EDGE,"E44.sketch_text.stroke-44"),sQuery(id+"F7.wireOp",EDGE,"E44.sketch_text.stroke-45"),sQuery(id+"F7.wireOp",EDGE,"E44.sketch_text.stroke-46"),sQuery(id+"F7.wireOp",EDGE,"E44.sketch_text.stroke-47"),sQuery(id+"F7.wireOp",EDGE,"E44.sketch_text.stroke-48"),sQuery(id+"F7.wireOp",EDGE,"E44.sketch_text.stroke-49"),sQuery(id+"F7.wireOp",EDGE,"E44.sketch_text.stroke-50"),sQuery(id+"F7.wireOp",EDGE,"E44.sketch_text.stroke-51"),sQuery(id+"F7.wireOp",EDGE,"E44.sketch_text.stroke-52"),sQuery(id+"F7.wireOp",EDGE,"E44.sketch_text.stroke-53"),sQuery(id+"F7.wireOp",EDGE,"E44.sketch_text.stroke-54"),sQuery(id+"F7.wireOp",EDGE,"E44.sketch_text.stroke-55"),sQuery(id+"F7.wireOp",EDGE,"E44.sketch_text.stroke-56")])]})});
            var Q8;
            Q8=makeQuery(id+"F8.split26.splitOp","SPLIT",BODY,{"derivedFrom":makeQuery(id+"F8.opExtrude","SWEPT_BODY",BODY,{"disambiguationData":[OSD([sQuery(id+"F7.wireOp",EDGE,"E44.sketch_text.stroke-57"),sQuery(id+"F7.wireOp",EDGE,"E44.sketch_text.stroke-58"),sQuery(id+"F7.wireOp",EDGE,"E44.sketch_text.stroke-59"),sQuery(id+"F7.wireOp",EDGE,"E44.sketch_text.stroke-60"),sQuery(id+"F7.wireOp",EDGE,"E44.sketch_text.stroke-61"),sQuery(id+"F7.wireOp",EDGE,"E44.sketch_text.stroke-62"),sQuery(id+"F7.wireOp",EDGE,"E44.sketch_text.stroke-63"),sQuery(id+"F7.wireOp",EDGE,"E44.sketch_text.stroke-64")])]})});
            var Q9;
            Q9=makeQuery(id+"F8.split27.splitOp","SPLIT",BODY,{"derivedFrom":makeQuery(id+"F8.opExtrude","SWEPT_BODY",BODY,{"disambiguationData":[OSD([sQuery(id+"F7.wireOp",EDGE,"E44.sketch_text.stroke-65"),sQuery(id+"F7.wireOp",EDGE,"E44.sketch_text.stroke-66"),sQuery(id+"F7.wireOp",EDGE,"E44.sketch_text.stroke-67"),sQuery(id+"F7.wireOp",EDGE,"E44.sketch_text.stroke-68"),sQuery(id+"F7.wireOp",EDGE,"E44.sketch_text.stroke-69"),sQuery(id+"F7.wireOp",EDGE,"E44.sketch_text.stroke-70"),sQuery(id+"F7.wireOp",EDGE,"E44.sketch_text.stroke-71"),sQuery(id+"F7.wireOp",EDGE,"E44.sketch_text.stroke-72"),sQuery(id+"F7.wireOp",EDGE,"E44.sketch_text.stroke-73"),sQuery(id+"F7.wireOp",EDGE,"E44.sketch_text.stroke-74"),sQuery(id+"F7.wireOp",EDGE,"E44.sketch_text.stroke-75"),sQuery(id+"F7.wireOp",EDGE,"E44.sketch_text.stroke-76")])]})});
            var Q10;
            Q10=makeQuery(id+"F8.split28.splitOp","SPLIT",BODY,{"derivedFrom":makeQuery(id+"F8.opExtrude","SWEPT_BODY",BODY,{"disambiguationData":[OSD([sQuery(id+"F7.wireOp",EDGE,"E45.sketch_text.stroke-0"),sQuery(id+"F7.wireOp",EDGE,"E45.sketch_text.stroke-1"),sQuery(id+"F7.wireOp",EDGE,"E45.sketch_text.stroke-2"),sQuery(id+"F7.wireOp",EDGE,"E45.sketch_text.stroke-3"),sQuery(id+"F7.wireOp",EDGE,"E45.sketch_text.stroke-4"),sQuery(id+"F7.wireOp",EDGE,"E45.sketch_text.stroke-5"),sQuery(id+"F7.wireOp",EDGE,"E45.sketch_text.stroke-6"),sQuery(id+"F7.wireOp",EDGE,"E45.sketch_text.stroke-7"),sQuery(id+"F7.wireOp",EDGE,"E45.sketch_text.stroke-8"),sQuery(id+"F7.wireOp",EDGE,"E45.sketch_text.stroke-9")])]})});
            var Q11;
            Q11=makeQuery(id+"F8.split29.splitOp","SPLIT",BODY,{"derivedFrom":makeQuery(id+"F8.opExtrude","SWEPT_BODY",BODY,{"disambiguationData":[OSD([sQuery(id+"F7.wireOp",EDGE,"E45.sketch_text.stroke-10"),sQuery(id+"F7.wireOp",EDGE,"E45.sketch_text.stroke-11"),sQuery(id+"F7.wireOp",EDGE,"E45.sketch_text.stroke-12"),sQuery(id+"F7.wireOp",EDGE,"E45.sketch_text.stroke-13"),sQuery(id+"F7.wireOp",EDGE,"E45.sketch_text.stroke-14"),sQuery(id+"F7.wireOp",EDGE,"E45.sketch_text.stroke-15"),sQuery(id+"F7.wireOp",EDGE,"E45.sketch_text.stroke-16"),sQuery(id+"F7.wireOp",EDGE,"E45.sketch_text.stroke-17"),sQuery(id+"F7.wireOp",EDGE,"E45.sketch_text.stroke-18"),sQuery(id+"F7.wireOp",EDGE,"E45.sketch_text.stroke-19"),sQuery(id+"F7.wireOp",EDGE,"E45.sketch_text.stroke-20"),sQuery(id+"F7.wireOp",EDGE,"E45.sketch_text.stroke-21")])]})});
            var Q12;
            Q12=makeQuery(id+"F8.split30.splitOp","SPLIT",BODY,{"derivedFrom":makeQuery(id+"F8.opExtrude","SWEPT_BODY",BODY,{"disambiguationData":[OSD([sQuery(id+"F7.wireOp",EDGE,"E45.sketch_text.stroke-22"),sQuery(id+"F7.wireOp",EDGE,"E45.sketch_text.stroke-23"),sQuery(id+"F7.wireOp",EDGE,"E45.sketch_text.stroke-24"),sQuery(id+"F7.wireOp",EDGE,"E45.sketch_text.stroke-25"),sQuery(id+"F7.wireOp",EDGE,"E45.sketch_text.stroke-26"),sQuery(id+"F7.wireOp",EDGE,"E45.sketch_text.stroke-27"),sQuery(id+"F7.wireOp",EDGE,"E45.sketch_text.stroke-28"),sQuery(id+"F7.wireOp",EDGE,"E45.sketch_text.stroke-29"),sQuery(id+"F7.wireOp",EDGE,"E45.sketch_text.stroke-30"),sQuery(id+"F7.wireOp",EDGE,"E45.sketch_text.stroke-31"),sQuery(id+"F7.wireOp",EDGE,"E45.sketch_text.stroke-32"),sQuery(id+"F7.wireOp",EDGE,"E45.sketch_text.stroke-33"),sQuery(id+"F7.wireOp",EDGE,"E45.sketch_text.stroke-34"),sQuery(id+"F7.wireOp",EDGE,"E45.sketch_text.stroke-35")])]})});
            var Q13;
            Q13=makeQuery(id+"F5.opBoolean","SPLIT",BODY,{"disambiguationData":[OD(1.0)],"derivedFrom":makeQuery(id+"F1.opExtrude","SWEPT_BODY",BODY,{"disambiguationData":[OSD([sQuery(id+"F0.wireOp",EDGE,"E0.left"),sQuery(id+"F0.wireOp",EDGE,"E0.right"),sQuery(id+"F0.wireOp",EDGE,"E3.rect.bottom"),sQuery(id+"F0.wireOp",EDGE,"E3.rect.top"),sQuery(id+"F0.wireOp",EDGE,"E3.rect.left"),sQuery(id+"F0.wireOp",EDGE,"E3.rect.right"),sQuery(id+"F0.wireOp",EDGE,"E4"),sQuery(id+"F0.wireOp",EDGE,"E6.MirrorC"),sQuery(id+"F0.wireOp",EDGE,"E7"),sQuery(id+"F0.wireOp",EDGE,"E8"),sQuery(id+"F0.wireOp",EDGE,"E9.rect.left"),sQuery(id+"F0.wireOp",EDGE,"E9.rect.right"),sQuery(id+"F0.wireOp",EDGE,"E10"),sQuery(id+"F0.wireOp",EDGE,"E11.MirrorC"),sQuery(id+"F0.wireOp",EDGE,"E9.rect.bottom"),sQuery(id+"F0.wireOp",EDGE,"E9.rect.top"),sQuery(id+"F0.wireOp",EDGE,"E12.rect.left"),sQuery(id+"F0.wireOp",EDGE,"E12.rect.right"),sQuery(id+"F0.wireOp",EDGE,"E13"),sQuery(id+"F0.wireOp",EDGE,"E14.MirrorC"),sQuery(id+"F0.wireOp",EDGE,"E12.rect.bottom"),sQuery(id+"F0.wireOp",EDGE,"E12.rect.top"),sQuery(id+"F0.wireOp",EDGE,"E15.rect.left"),sQuery(id+"F0.wireOp",EDGE,"E15.rect.right"),sQuery(id+"F0.wireOp",EDGE,"E16"),sQuery(id+"F0.wireOp",EDGE,"E17.MirrorC"),sQuery(id+"F0.wireOp",EDGE,"E15.rect.bottom"),sQuery(id+"F0.wireOp",EDGE,"E15.rect.top"),sQuery(id+"F0.wireOp",EDGE,"E18.rect.left"),sQuery(id+"F0.wireOp",EDGE,"E18.rect.right"),sQuery(id+"F0.wireOp",EDGE,"E19"),sQuery(id+"F0.wireOp",EDGE,"E20.MirrorC"),sQuery(id+"F0.wireOp",EDGE,"E18.rect.bottom"),sQuery(id+"F0.wireOp",EDGE,"E18.rect.top")])]})});
            booleanBodies(context, id + "F10", {"operationType" : BooleanOperationType.SUBTRACTION, "tools" : qUnion([Q0, Q1, Q2, Q3, Q4, Q5, Q6, Q7, Q8, Q9, Q10, Q11, Q12]), "targets" : qUnion([Q13]), "keepTools" : true});
        }
        {
            var Q0;
            Q0=makeQuery(id+"F8.opExtrude","CAP_FACE",FACE,{"disambiguationData":[OSD([sQuery(id+"F7.wireOp",EDGE,"E40.sketch_text.stroke-0"),sQuery(id+"F7.wireOp",EDGE,"E40.sketch_text.stroke-1"),sQuery(id+"F7.wireOp",EDGE,"E40.sketch_text.stroke-2"),sQuery(id+"F7.wireOp",EDGE,"E40.sketch_text.stroke-3"),sQuery(id+"F7.wireOp",EDGE,"E40.sketch_text.stroke-4"),sQuery(id+"F7.wireOp",EDGE,"E40.sketch_text.stroke-5"),sQuery(id+"F7.wireOp",EDGE,"E40.sketch_text.stroke-6"),sQuery(id+"F7.wireOp",EDGE,"E40.sketch_text.stroke-7"),sQuery(id+"F7.wireOp",EDGE,"E40.sketch_text.stroke-8"),sQuery(id+"F7.wireOp",EDGE,"E40.sketch_text.stroke-9"),sQuery(id+"F7.wireOp",EDGE,"E40.sketch_text.stroke-10"),sQuery(id+"F7.wireOp",EDGE,"E40.sketch_text.stroke-11"),sQuery(id+"F7.wireOp",EDGE,"E40.sketch_text.stroke-12"),sQuery(id+"F7.wireOp",EDGE,"E40.sketch_text.stroke-13")])],"isStart":false});
            var sketch = newSketch(context, id + "F11", { "sketchPlane" : qUnion([Q0])});
            skLineSegment(sketch, "E46.bottom", {"start": v(-345.5, 65.3) * mm, "end": v(61.6, 65.3) * mm});
            skLineSegment(sketch, "E46.top", {"start": v(-345.5, -70.6) * mm, "end": v(61.6, -70.6) * mm});
            skLineSegment(sketch, "E46.left", {"start": v(-345.5, 65.3) * mm, "end": v(-345.5, -70.6) * mm});
            skLineSegment(sketch, "E46.right", {"start": v(61.6, 65.3) * mm, "end": v(61.6, -70.6) * mm});
            skSolve(sketch);
        }
        {
            var Q0;
            Q0 = qSketchRegion(id + "F11", true);
            extrude(context, id + "F12", {"entities" : qUnion([Q0]), "oppositeDirection" : true, "depth" : 0.89 * mm, "symmetric" : true});
        }
    });
